# Revit family: Windows_Pruso_LK78_P50L-Facade_Single-Sash_Outward-Opening-Window-84mm
name_source: partatom
category: Windows
revit_build: Autodesk Revit 2018 (Build: 20170223_1515(x64)
units: mm (PartAtom-declared; Revit-internal decimal feet)

## family parameters
Always vertical = Yes
Cut with Voids When Loaded = No
OmniClass Number = 23.30.20.00
OmniClass Title = Windows
Room Calculation Point = No
Shared = No

## types (1)
- Windows_Pruso_LK78_P50L-Facade_Single-Sash_Outward-Opening-Window-84mm
    Assembly Code = B2020100
    Description = LK78 P50L Facade Single Sash Inward Opening Window 68mm
    Edition number = 1
    Frame Material = Default
    Handle Material = Aluminium - Purso - Aluminium
    Keynote = 08500
    Leaf Material = Default
    Manufacturer = Purso
    Model = LK78 P50L Facade Single Sash Inward Opening Window 68mm
    Product Guid = 730e73cb-869f-4c9c-b009-8c912971387c
    Product data url = https://www.bimobject.com
    URL = https://purso.fi

## geometry (parser evidence)
native form markers: Sweep x7
no freeform markers — native parametric forms only
